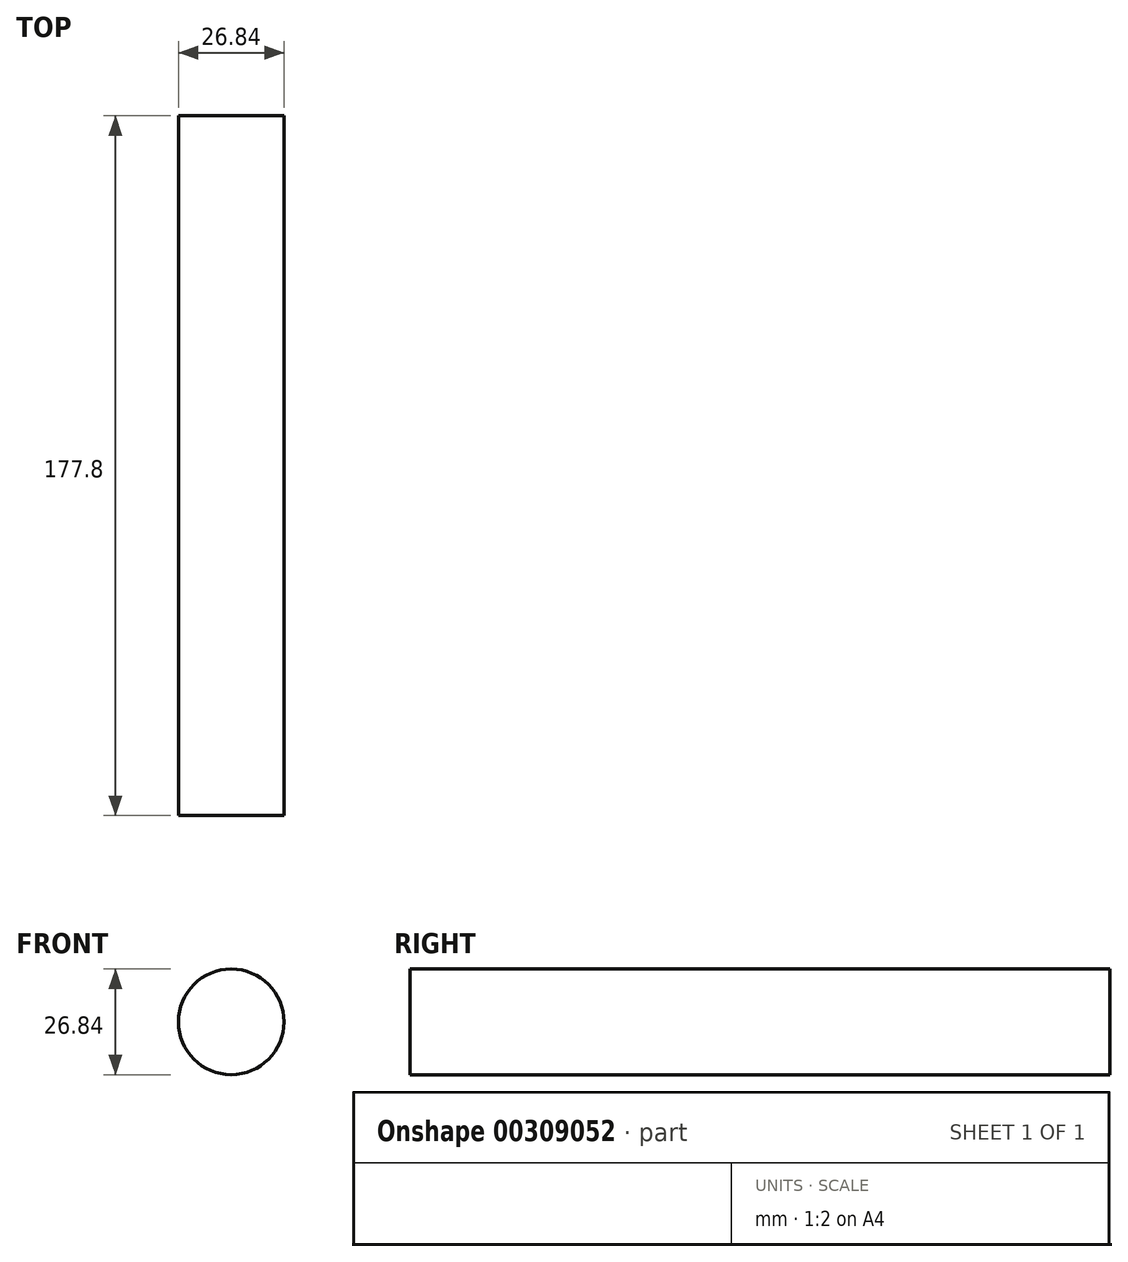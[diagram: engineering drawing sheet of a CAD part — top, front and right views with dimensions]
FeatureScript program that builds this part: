
annotation { "Feature Type Name" : "Feature", "Feature Type Description" : "" }
export const myFeature = defineFeature(function(context is Context, id is Id, definition is map)
    precondition{}
    {
        {
            var Q0;
            Q0=qCreatedBy(makeId("Front.planeOp"),FACE);
            var sketch = newSketch(context, id + "F0", { "sketchPlane" : qUnion([Q0])});
            skCircle(sketch, "E0", {"center": v(0, 0) * mm, "radius": 13.42 * mm});
            skCircle(sketch, "E1", {"center": v(37.46, 0) * mm, "radius": 10.44 * mm});
            skSolve(sketch);
        }
        {
            var Q0;
            Q0=makeQuery(id+"F0.imprint","IMPRINT",FACE,{"disambiguationData":[TD([[makeQuery(id+"F0.imprint","IMPRINT",EDGE,{"derivedFrom":sQuery(id+"F0.wireOp",EDGE,"E0")}),1.0]])]});
            var Q1;
            Q1=makeQuery(id+"F0.imprint","IMPRINT",FACE,{"disambiguationData":[TD([[makeQuery(id+"F0.imprint","IMPRINT",EDGE,{"derivedFrom":sQuery(id+"F0.wireOp",EDGE,"E1")}),1.0]])]});
            extrude(context, id + "F1", {"entities" : qUnion([Q0, Q1]), "depth" : 177.8 * mm});
        }
        {
            var Q0;
            Q0=makeQuery(id+"F1.opExtrude","CAP_FACE",FACE,{"disambiguationData":[OSD([sQuery(id+"F0.wireOp",EDGE,"E0")])],"isStart":false});
            var sketch = newSketch(context, id + "F2", { "sketchPlane" : qUnion([Q0])});
            skLineSegment(sketch, "E2.bottom", {"start": v(-17.56, 15.3) * mm, "end": v(55.93, 15.3) * mm});
            skLineSegment(sketch, "E2.top", {"start": v(-17.56, -18.68) * mm, "end": v(55.93, -18.68) * mm});
            skLineSegment(sketch, "E2.left", {"start": v(-17.56, 15.3) * mm, "end": v(-17.56, -18.68) * mm});
            skLineSegment(sketch, "E2.right", {"start": v(55.93, 15.3) * mm, "end": v(55.93, -18.68) * mm});
            skSolve(sketch);
        }
        {
            var Q0;
            Q0=makeQuery(id+"F2.imprint","IMPRINT",FACE,{"disambiguationData":[TD([[makeQuery(id+"F2.imprint","IMPRINT",EDGE,{"derivedFrom":sQuery(id+"F2.wireOp",EDGE,"E2.bottom")}),-1.0]])]});
            extrude(context, id + "F3", {"entities" : qUnion([Q0]), "operationType" : NewBodyOperationType.ADD, "depth" : 25.4 * mm});
        }
        {
            var Q0;
            {var subQ0=sQuery(id+"F0.wireOp",EDGE,"E0");Q0=makeQuery(id+"F3.boolean.opBoolean","MERGE",BODY,{"derivedFrom":[makeQuery(id+"F1.opExtrude","SWEPT_BODY",BODY,{"disambiguationData":[OSD([subQ0])]}),makeQuery(id+"F1.opExtrude","SWEPT_BODY",BODY,{"disambiguationData":[OSD([sQuery(id+"F0.wireOp",EDGE,"E1")])]}),makeQuery(id+"F3.opExtrude","SWEPT_BODY",BODY,{"disambiguationData":[OSD([subQ0,sQuery(id+"F2.wireOp",EDGE,"E2.bottom"),sQuery(id+"F2.wireOp",EDGE,"E2.top"),sQuery(id+"F2.wireOp",EDGE,"E2.left"),sQuery(id+"F2.wireOp",EDGE,"E2.right")])]})]});}
            deleteBodies(context, id + "F4", {"entities" : qUnion([Q0])});
        }
    });
